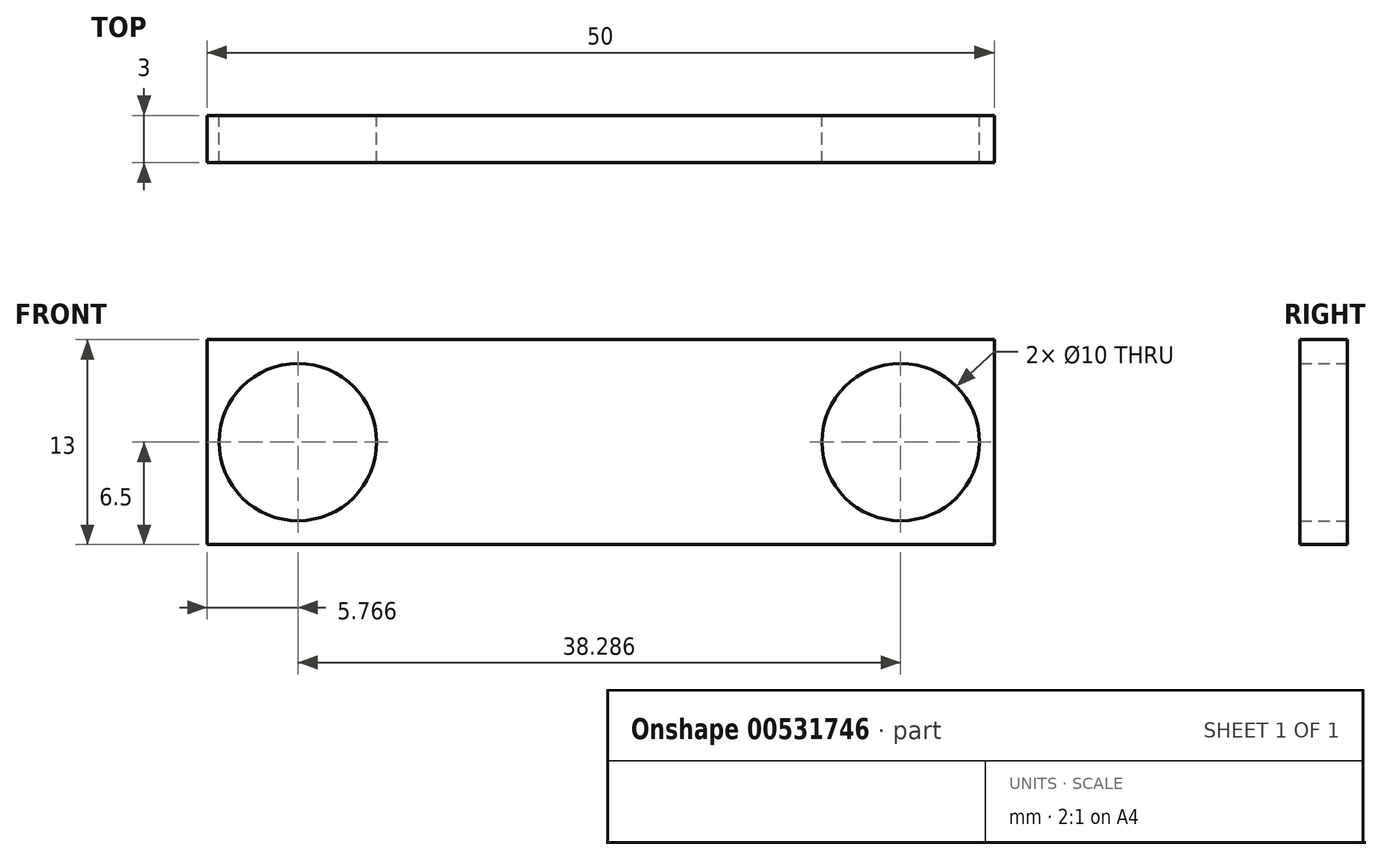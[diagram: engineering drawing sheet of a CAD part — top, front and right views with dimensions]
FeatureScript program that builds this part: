
annotation { "Feature Type Name" : "Feature", "Feature Type Description" : "" }
export const myFeature = defineFeature(function(context is Context, id is Id, definition is map)
    precondition{}
    {
        {
            var Q0;
            Q0=qCreatedBy(makeId("Front.planeOp"),FACE);
            var sketch = newSketch(context, id + "F0", { "sketchPlane" : qUnion([Q0])});
            skLineSegment(sketch, "E0.bottom", {"start": v(25, -6.5) * mm, "end": v(-25, -6.5) * mm});
            skLineSegment(sketch, "E0.top", {"start": v(25, 6.5) * mm, "end": v(-25, 6.5) * mm});
            skLineSegment(sketch, "E0.left", {"start": v(25, -6.5) * mm, "end": v(25, 6.5) * mm});
            skLineSegment(sketch, "E0.right", {"start": v(-25, -6.5) * mm, "end": v(-25, 6.5) * mm});
            skPoint(sketch, "E0.middle", {"position": v(0, 0) * mm});
            skCircle(sketch, "E1", {"center": v(-19.23, 0) * mm, "radius": 5 * mm});
            skCircle(sketch, "E2", {"center": v(19.05, 0) * mm, "radius": 5 * mm});
            skSolve(sketch);
        }
        {
            var Q0;
            Q0=makeQuery(id+"F0.imprint","IMPRINT",FACE,{"disambiguationData":[TD([[makeQuery(id+"F0.imprint","IMPRINT",EDGE,{"derivedFrom":sQuery(id+"F0.wireOp",EDGE,"E0.bottom")}),-1.0]])]});
            extrude(context, id + "F1", {"entities" : qUnion([Q0]), "depth" : 3 * mm, "offsetDistance" : 25 * mm});
        }
    });
